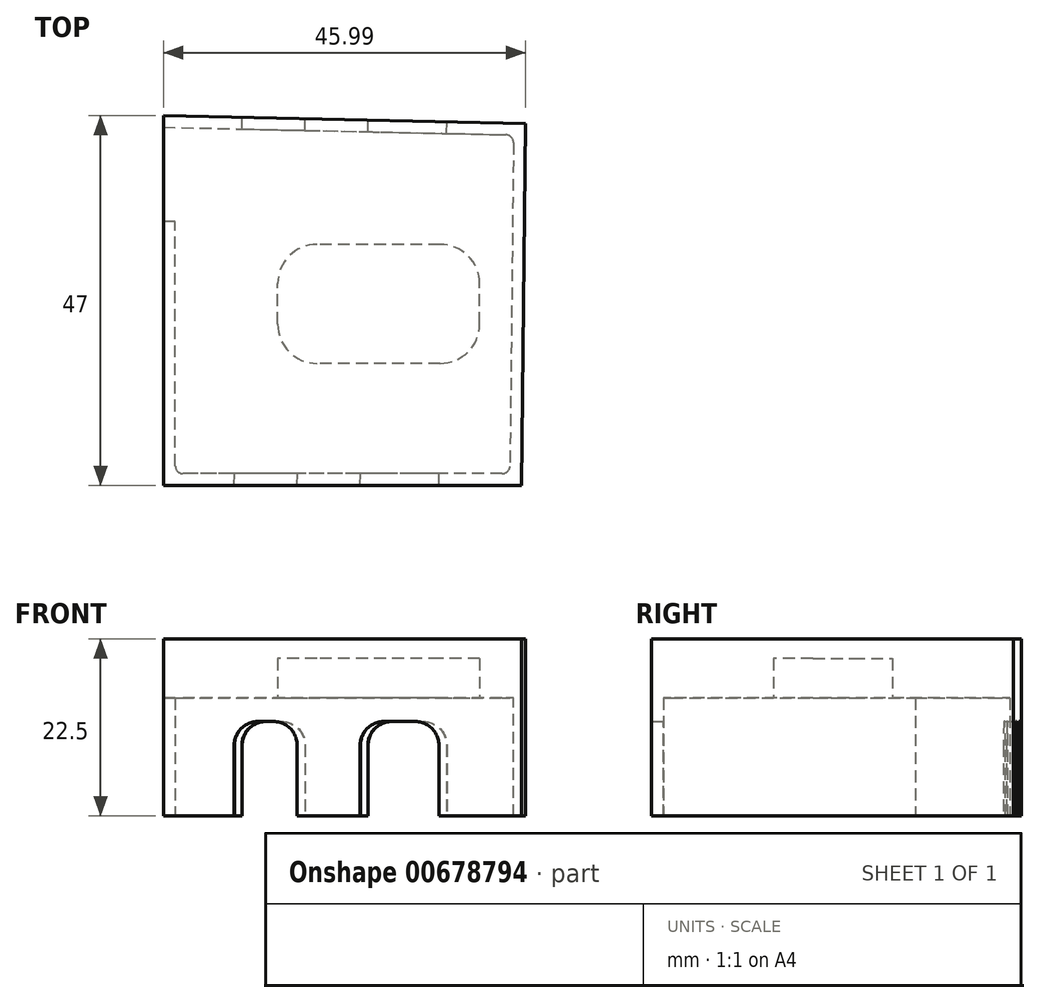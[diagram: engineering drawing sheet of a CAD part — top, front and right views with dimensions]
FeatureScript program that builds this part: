
annotation { "Feature Type Name" : "Feature", "Feature Type Description" : "" }
export const myFeature = defineFeature(function(context is Context, id is Id, definition is map)
    precondition{}
    {
        {
            var Q0;
            Q0=qCreatedBy(makeId("Top.planeOp"),FACE);
            var sketch = newSketch(context, id + "F0", { "sketchPlane" : qUnion([Q0])});
            skLineSegment(sketch, "E0", {"start": v(0, 0) * mm, "end": v(45.5, 0) * mm});
            skLineSegment(sketch, "E1", {"start": v(0, 0) * mm, "end": v(0, 47) * mm});
            skLineSegment(sketch, "E2", {"start": v(45.5, 0) * mm, "end": v(45.99, 46) * mm});
            skLineSegment(sketch, "E3", {"start": v(45.99, 46) * mm, "end": v(0, 47) * mm});
            skSolve(sketch);
        }
        {
            var Q0;
            Q0=makeQuery(id+"F0.imprint","IMPRINT",FACE,{"disambiguationData":[TD([[makeQuery(id+"F0.imprint","IMPRINT",EDGE,{"derivedFrom":sQuery(id+"F0.wireOp",EDGE,"E0")}),1.0]])]});
            extrude(context, id + "F1", {"entities" : qUnion([Q0]), "depth" : 22.5 * mm, "offsetDistance" : 25 * mm});
        }
        {
            var Q0;
            Q0=qCreatedBy(makeId("Top.planeOp"),FACE);
            var sketch = newSketch(context, id + "F2", { "sketchPlane" : qUnion([Q0])});
            skLineSegment(sketch, "E4", {"start": v(1.5, 1.5) * mm, "end": v(1.5, 33.5) * mm});
            skLineSegment(sketch, "E5", {"start": v(1.5, 33.5) * mm, "end": v(0, 33.5) * mm});
            skLineSegment(sketch, "E6", {"start": v(0, 33.5) * mm, "end": v(0, 45.5) * mm});
            skLineSegment(sketch, "E7", {"start": v(0, 45.5) * mm, "end": v(44.47, 44.53) * mm});
            skLineSegment(sketch, "E8", {"start": v(44.47, 44.53) * mm, "end": v(44, 1.5) * mm});
            skLineSegment(sketch, "E9", {"start": v(44, 1.5) * mm, "end": v(1.5, 1.5) * mm});
            skSolve(sketch);
        }
        {
            var Q0;
            Q0=makeQuery(id+"F2.imprint","IMPRINT",FACE,{"disambiguationData":[TD([[makeQuery(id+"F2.imprint","IMPRINT",EDGE,{"derivedFrom":sQuery(id+"F2.wireOp",EDGE,"E4")}),-1.0]])]});
            extrude(context, id + "F3", {"entities" : qUnion([Q0]), "operationType" : NewBodyOperationType.REMOVE, "depth" : 15 * mm, "offsetDistance" : 25 * mm});
        }
        {
            var Q0;
            Q0=makeQuery(id+"F3.boolean.opBoolean","COPY",FACE,{"derivedFrom":makeQuery(id+"F3.opExtrude","CAP_FACE",FACE,{"disambiguationData":[OSD([sQuery(id+"F2.wireOp",EDGE,"E4"),sQuery(id+"F2.wireOp",EDGE,"E5"),sQuery(id+"F2.wireOp",EDGE,"E6"),sQuery(id+"F2.wireOp",EDGE,"E7"),sQuery(id+"F2.wireOp",EDGE,"E8"),sQuery(id+"F2.wireOp",EDGE,"E9")])],"isStart":false})});
            var sketch = newSketch(context, id + "F4", { "sketchPlane" : qUnion([Q0])});
            skLineSegment(sketch, "E10.bottom", {"start": v(40.16, -30.62) * mm, "end": v(14.5, -30.62) * mm});
            skLineSegment(sketch, "E10.top", {"start": v(40.16, -15.5) * mm, "end": v(14.5, -15.5) * mm});
            skLineSegment(sketch, "E10.left", {"start": v(14.5, -15.5) * mm, "end": v(14.5, -30.62) * mm});
            skLineSegment(sketch, "E10.right", {"start": v(40.16, -15.5) * mm, "end": v(40.16, -30.62) * mm});
            skSolve(sketch);
        }
        {
            var Q0;
            Q0 = qSketchRegion(id + "F4", true);
            extrude(context, id + "F5", {"entities" : qUnion([Q0]), "operationType" : NewBodyOperationType.REMOVE, "oppositeDirection" : true, "depth" : 5 * mm, "offsetDistance" : 25 * mm});
        }
        {
            var Q0;
            Q0=makeQuery(id+"F5.boolean.opBoolean","COPY",EDGE,{"derivedFrom":makeQuery(id+"F5.opExtrude","SWEPT_EDGE",EDGE,{"disambiguationData":[OSD([sQuery(id+"F4.wireOp",EDGE,"E10.bottom"),sQuery(id+"F4.wireOp",EDGE,"E10.left")])]})});
            var Q1;
            Q1=makeQuery(id+"F5.boolean.opBoolean","COPY",EDGE,{"derivedFrom":makeQuery(id+"F5.opExtrude","SWEPT_EDGE",EDGE,{"disambiguationData":[OSD([sQuery(id+"F4.wireOp",EDGE,"E10.bottom"),sQuery(id+"F4.wireOp",EDGE,"E10.right")])]})});
            var Q2;
            Q2=makeQuery(id+"F5.boolean.opBoolean","COPY",EDGE,{"derivedFrom":makeQuery(id+"F5.opExtrude","SWEPT_EDGE",EDGE,{"disambiguationData":[OSD([sQuery(id+"F4.wireOp",EDGE,"E10.top"),sQuery(id+"F4.wireOp",EDGE,"E10.left")])]})});
            var Q3;
            Q3=makeQuery(id+"F5.boolean.opBoolean","COPY",EDGE,{"derivedFrom":makeQuery(id+"F5.opExtrude","SWEPT_EDGE",EDGE,{"disambiguationData":[OSD([sQuery(id+"F4.wireOp",EDGE,"E10.top"),sQuery(id+"F4.wireOp",EDGE,"E10.right")])]})});
            fillet(context, id + "F6", {"entities" : qUnion([Q0, Q1, Q2, Q3]), "radius" : 5 * mm, "tangentPropagation" : true, "allowEdgeOverflow" : false});
        }
        {
            var Q0;
            Q0=makeQuery(id+"F1.opExtrude","SWEPT_FACE",FACE,{"disambiguationData":[OSD([sQuery(id+"F0.wireOp",EDGE,"E3")])]});
            var sketch = newSketch(context, id + "F7", { "sketchPlane" : qUnion([Q0])});
            skLineSegment(sketch, "E11", {"start": v(-8.98, 0) * mm, "end": v(-8.98, 9) * mm});
            skLineSegment(sketch, "E12", {"start": v(-11.98, 12) * mm, "end": v(-13.98, 12) * mm});
            skLineSegment(sketch, "E13", {"start": v(-16.98, 9) * mm, "end": v(-16.98, 0) * mm});
            skLineSegment(sketch, "E14", {"start": v(-24.98, 0) * mm, "end": v(-24.98, 9) * mm});
            skLineSegment(sketch, "E15", {"start": v(-27.98, 12) * mm, "end": v(-31.98, 12) * mm});
            skLineSegment(sketch, "E16", {"start": v(-34.98, 9) * mm, "end": v(-34.98, 0) * mm});
            skLineSegment(sketch, "E17", {"start": v(-16.98, 0) * mm, "end": v(-8.98, 0) * mm});
            skLineSegment(sketch, "E18", {"start": v(-34.98, 0) * mm, "end": v(-24.98, 0) * mm});
            skPoint(sketch, "E19.visualSharp", {"position": v(-8.98, 12) * mm});
            skArc(sketch, "E19.filletArc", {"start": v(-8.98, 9) * mm, "mid": v(-9.85, 11.12) * mm, "end": v(-11.98, 12) * mm});
            skPoint(sketch, "E20.visualSharp", {"position": v(-16.98, 12) * mm});
            skArc(sketch, "E20.filletArc", {"start": v(-13.98, 12) * mm, "mid": v(-16.1, 11.12) * mm, "end": v(-16.98, 9) * mm});
            skPoint(sketch, "E21.visualSharp", {"position": v(-24.98, 12) * mm});
            skArc(sketch, "E21.filletArc", {"start": v(-24.98, 9) * mm, "mid": v(-25.85, 11.12) * mm, "end": v(-27.98, 12) * mm});
            skPoint(sketch, "E22.visualSharp", {"position": v(-34.98, 12) * mm});
            skArc(sketch, "E22.filletArc", {"start": v(-31.98, 12) * mm, "mid": v(-34.1, 11.12) * mm, "end": v(-34.98, 9) * mm});
            skSolve(sketch);
        }
        {
            var Q0;
            Q0 = qSketchRegion(id + "F7", true);
            extrude(context, id + "F8", {"entities" : qUnion([Q0]), "operationType" : NewBodyOperationType.REMOVE, "endBound" : BoundingType.THROUGH_ALL, "oppositeDirection" : true, "depth" : 25 * mm, "offsetDistance" : 25 * mm});
        }
        {
            var Q0;
            Q0=makeQuery(id+"F3.boolean.opBoolean","COPY",EDGE,{"derivedFrom":makeQuery(id+"F3.opExtrude","SWEPT_EDGE",EDGE,{"disambiguationData":[OSD([sQuery(id+"F2.wireOp",EDGE,"E4"),sQuery(id+"F2.wireOp",EDGE,"E9")])]})});
            var Q1;
            Q1=makeQuery(id+"F3.boolean.opBoolean","COPY",EDGE,{"derivedFrom":makeQuery(id+"F3.opExtrude","SWEPT_EDGE",EDGE,{"disambiguationData":[OSD([sQuery(id+"F2.wireOp",EDGE,"E8"),sQuery(id+"F2.wireOp",EDGE,"E9")])]})});
            var Q2;
            Q2=makeQuery(id+"F3.boolean.opBoolean","COPY",EDGE,{"derivedFrom":makeQuery(id+"F3.opExtrude","SWEPT_EDGE",EDGE,{"disambiguationData":[OSD([sQuery(id+"F2.wireOp",EDGE,"E7"),sQuery(id+"F2.wireOp",EDGE,"E8")])]})});
            fillet(context, id + "F9", {"entities" : qUnion([Q0, Q1, Q2]), "radius" : 1 * mm, "tangentPropagation" : true, "allowEdgeOverflow" : false});
        }
    });
